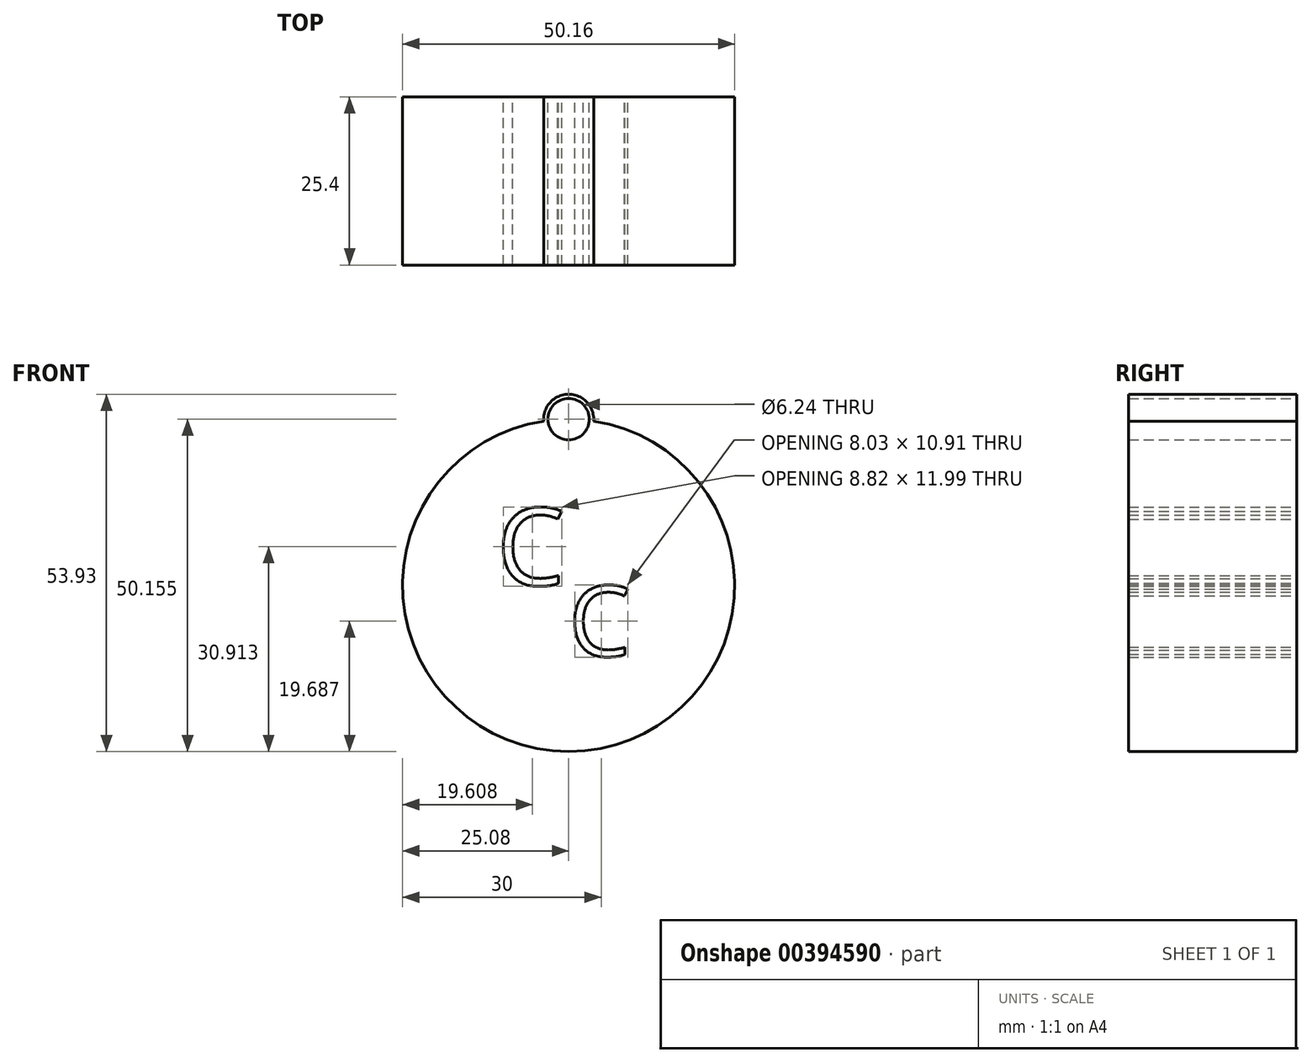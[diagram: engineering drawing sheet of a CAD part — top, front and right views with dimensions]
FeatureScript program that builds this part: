
annotation { "Feature Type Name" : "Feature", "Feature Type Description" : "" }
export const myFeature = defineFeature(function(context is Context, id is Id, definition is map)
    precondition{}
    {
        {
            var Q0;
            Q0=qCreatedBy(makeId("Front.planeOp"),FACE);
            var sketch = newSketch(context, id + "F0", { "sketchPlane" : qUnion([Q0])});
            skArc(sketch, "E0", {"start": v(-3.76, 24.8) * mm, "mid": v(0, -25.08) * mm, "end": v(3.76, 24.8) * mm});
            skText(sketch, "E1", { "text": "C\n", "fontName": "OpenSans-Regular.ttf"});
            skText(sketch, "E2", { "text": "C\n", "fontName": "OpenSans-Regular.ttf"});
            skCircle(sketch, "E3", {"center": v(0, 25.08) * mm, "radius": 3.77 * mm});
            skCircle(sketch, "E4", {"center": v(0, 25.08) * mm, "radius": 3.12 * mm});
            const initialGuessF0  = {"E1": [-0.01088, 0, 1, 0, 0.01176], "E2": [0, -0.0107, 1, 0, 0.0107]};
            skSetInitialGuess(sketch, initialGuessF0);
            skSolve(sketch);
        }
        {
            var Q0;
            {var subQ0=sQuery(id+"F0.wireOp",EDGE,"E0");Q0=makeQuery(id+"F0.imprint","IMPRINT",FACE,{"disambiguationData":[TD([[makeQuery(id+"F0.imprint","IMPRINT",EDGE,{"derivedFrom":subQ0}),1.0]])]});}
            var Q1;
            Q1=makeQuery(id+"F0.imprint","IMPRINT",FACE,{"disambiguationData":[TD([[makeQuery(id+"F0.imprint","IMPRINT",EDGE,{"derivedFrom":sQuery(id+"F0.wireOp",EDGE,"E4")}),-1.0]])]});
            extrude(context, id + "F1", {"entities" : qUnion([Q0, Q1]), "depth" : 25.4 * mm});
        }
    });
